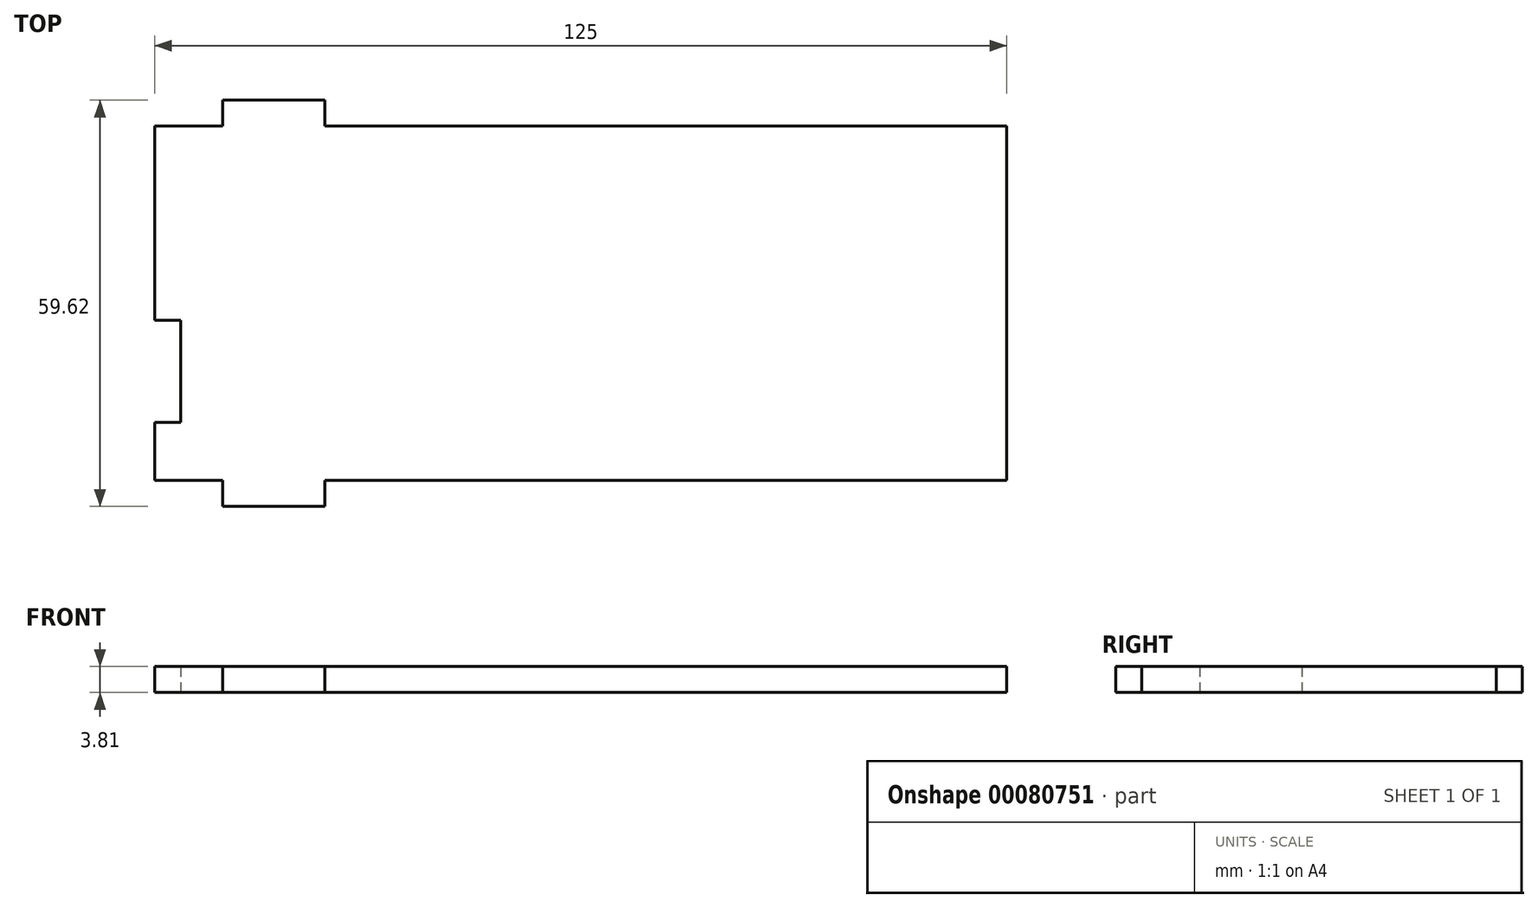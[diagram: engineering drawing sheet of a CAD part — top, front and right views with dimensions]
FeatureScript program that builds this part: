
annotation { "Feature Type Name" : "Feature", "Feature Type Description" : "" }
export const myFeature = defineFeature(function(context is Context, id is Id, definition is map)
    precondition{}
    {
        {
            var Q0;
            Q0=qCreatedBy(makeId("Top.planeOp"),FACE);
            var sketch = newSketch(context, id + "F0", { "sketchPlane" : qUnion([Q0])});
            skLineSegment(sketch, "E0.bottom", {"start": v(62.5, 26) * mm, "end": v(-62.5, 26) * mm});
            skLineSegment(sketch, "E0.top", {"start": v(62.5, -26) * mm, "end": v(-62.5, -26) * mm});
            skLineSegment(sketch, "E0.left", {"start": v(62.5, 26) * mm, "end": v(62.5, -26) * mm});
            skLineSegment(sketch, "E0.right", {"start": v(-62.5, 26) * mm, "end": v(-62.5, -26) * mm});
            skPoint(sketch, "E0.middle", {"position": v(0, 0) * mm});
            skLineSegment(sketch, "E1", {"start": v(-62.5, 0) * mm, "end": v(0, 0) * mm, "construction": true});
            skLineSegment(sketch, "E2", {"start": v(-52.5, -26) * mm, "end": v(-52.5, -29.8) * mm});
            skLineSegment(sketch, "E3", {"start": v(-52.5, -29.8) * mm, "end": v(-37.5, -29.8) * mm});
            skLineSegment(sketch, "E4", {"start": v(-37.5, -29.8) * mm, "end": v(-37.5, -26) * mm});
            skLineSegment(sketch, "E5.MirrorCS", {"start": v(-52.5, 26) * mm, "end": v(-52.5, 29.8) * mm});
            skLineSegment(sketch, "E6.MirrorCS", {"start": v(-37.5, 29.8) * mm, "end": v(-37.5, 26) * mm});
            skLineSegment(sketch, "E7.MirrorCS", {"start": v(-52.5, 29.8) * mm, "end": v(-37.5, 29.8) * mm});
            skLineSegment(sketch, "E8", {"start": v(-62.5, -2.5) * mm, "end": v(-58.7, -2.5) * mm});
            skLineSegment(sketch, "E9", {"start": v(-58.7, -2.5) * mm, "end": v(-58.7, -17.5) * mm});
            skLineSegment(sketch, "E10", {"start": v(-58.7, -17.5) * mm, "end": v(-62.5, -17.5) * mm});
            skSolve(sketch);
        }
        {
            var Q0;
            Q0=makeQuery(id+"F0.imprint","IMPRINT",FACE,{"disambiguationData":[TD([[makeQuery(id+"F0.imprint","IMPRINT",EDGE,{"derivedFrom":sQuery(id+"F0.wireOp",EDGE,"E0.bottom")}),1.0]])]});
            var Q1;
            {var subQ0=sQuery(id+"F0.wireOp",EDGE,"E5.MirrorCS");Q1=makeQuery(id+"F0.imprint","IMPRINT",FACE,{"disambiguationData":[TD([[makeQuery(id+"F0.imprint","IMPRINT",EDGE,{"derivedFrom":subQ0}),-1.0]])]});}
            var Q2;
            {var subQ0=sQuery(id+"F0.wireOp",EDGE,"E2");Q2=makeQuery(id+"F0.imprint","IMPRINT",FACE,{"disambiguationData":[TD([[makeQuery(id+"F0.imprint","IMPRINT",EDGE,{"derivedFrom":subQ0}),1.0]])]});}
            extrude(context, id + "F1", {"entities" : qUnion([Q0, Q1, Q2]), "depth" : 3.8 * mm});
        }
    });
